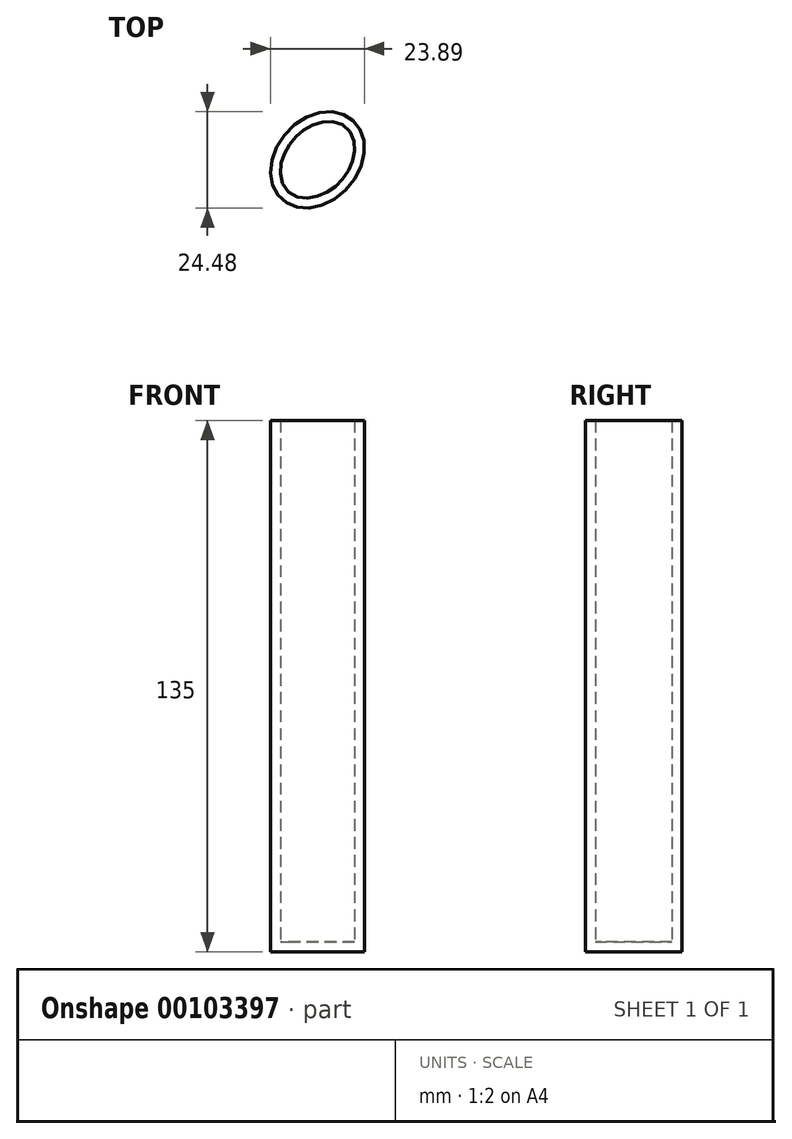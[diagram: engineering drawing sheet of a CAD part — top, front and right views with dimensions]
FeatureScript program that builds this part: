
annotation { "Feature Type Name" : "Feature", "Feature Type Description" : "" }
export const myFeature = defineFeature(function(context is Context, id is Id, definition is map)
    precondition{}
    {
        {
            var Q0;
            Q0=qCreatedBy(makeId("Top.planeOp"),FACE);
            var sketch = newSketch(context, id + "F0", { "sketchPlane" : qUnion([Q0])});
            skEllipse(sketch, "E0", {"center": v(-55.2, 46.09) * mm, "majorRadius": 13.5 * mm, "minorRadius": 10.5 * mm, "majorAxis": v(0.67, 0.74)});
            skSolve(sketch);
        }
        {
            var Q0;
            Q0 = qSketchRegion(id + "F0", true);
            extrude(context, id + "F1", {"entities" : qUnion([Q0]), "depth" : 135 * mm});
        }
        {
            var Q0;
            Q0=makeQuery(id+"F1.opExtrude","CAP_FACE",FACE,{"disambiguationData":[OSD([sQuery(id+"F0.wireOp",EDGE,"E0")])],"isStart":false});
            shell(context, id + "F2", {"entities" : qUnion([Q0]), "thickness" : 2.5 * mm});
        }
    });
